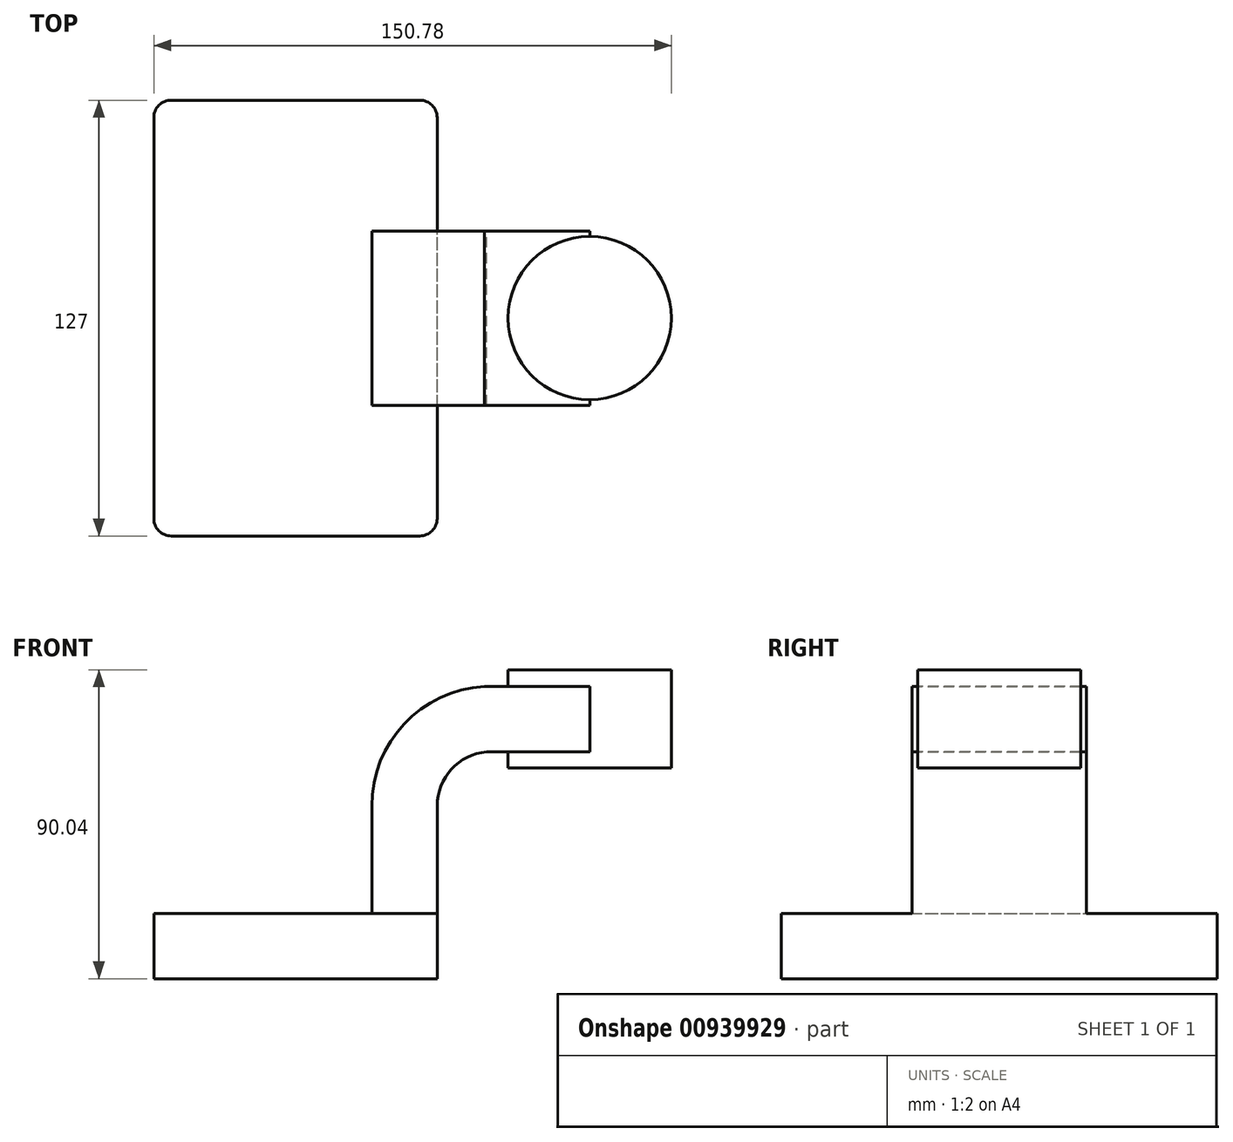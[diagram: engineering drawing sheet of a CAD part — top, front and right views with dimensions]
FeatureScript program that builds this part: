
annotation { "Feature Type Name" : "Feature", "Feature Type Description" : "" }
export const myFeature = defineFeature(function(context is Context, id is Id, definition is map)
    precondition{}
    {
        {
            var Q0;
            Q0=qCreatedBy(makeId("Front.planeOp"),FACE);
            var sketch = newSketch(context, id + "F0", { "sketchPlane" : qUnion([Q0])});
            skLineSegment(sketch, "E0.bottom", {"start": v(41.27, 9.53) * mm, "end": v(-41.28, 9.53) * mm});
            skLineSegment(sketch, "E0.top", {"start": v(41.28, -9.52) * mm, "end": v(-41.27, -9.52) * mm});
            skLineSegment(sketch, "E0.left", {"start": v(41.28, 9.53) * mm, "end": v(41.28, -9.52) * mm});
            skLineSegment(sketch, "E0.right", {"start": v(-41.28, 9.53) * mm, "end": v(-41.27, -9.52) * mm});
            skPoint(sketch, "E0.middle", {"position": v(0, 0) * mm});
            skLineSegment(sketch, "E1", {"start": v(41.27, 9.53) * mm, "end": v(41.27, 40.78) * mm});
            skArc(sketch, "E2", {"start": v(41.27, 40.78) * mm, "mid": v(45.42, 51.48) * mm, "end": v(55.7, 56.6) * mm});
            skLineSegment(sketch, "E3", {"start": v(55.7, 56.6) * mm, "end": v(85.73, 56.6) * mm});
            skPoint(sketch, "E4.middle", {"position": v(72.16, 48.26) * mm});
            skLineSegment(sketch, "E5.0", {"start": v(55, 75.64) * mm, "end": v(85.73, 75.64) * mm});
            skArc(sketch, "E5.1", {"start": v(22.23, 40.78) * mm, "mid": v(31.7, 64.7) * mm, "end": v(55, 75.64) * mm});
            skLineSegment(sketch, "E5.2", {"start": v(22.23, 9.53) * mm, "end": v(22.23, 40.78) * mm});
            skLineSegment(sketch, "E6.bottom", {"start": v(58.7, 51.93) * mm, "end": v(109.5, 51.93) * mm});
            skLineSegment(sketch, "E6.top", {"start": v(58.7, 80.5) * mm, "end": v(109.5, 80.5) * mm});
            skLineSegment(sketch, "E6.left", {"start": v(58.7, 51.93) * mm, "end": v(58.7, 80.5) * mm});
            skLineSegment(sketch, "E6.right", {"start": v(109.5, 51.93) * mm, "end": v(109.5, 80.5) * mm});
            skLineSegment(sketch, "E7", {"start": v(85.73, 80.5) * mm, "end": v(85.73, 51.93) * mm});
            skFitSpline(sketch, "E8", {"points": [v(-41.28, 9.53) * mm, v(58.7, 80.5) * mm], "startDerivative": vector(30.6, 76.42) * mm, "endDerivative": vector(213.62, 12.05) * mm});
            skSolve(sketch);
        }
        {
            var Q0;
            Q0=makeQuery(id+"F0.imprint","IMPRINT",FACE,{"disambiguationData":[TD([[makeQuery(id+"F0.imprint","IMPRINT",EDGE,{"derivedFrom":sQuery(id+"F0.wireOp",EDGE,"E0.top")}),-1.0]])]});
            extrude(context, id + "F1", {"entities" : qUnion([Q0]), "depth" : 127 * mm, "offsetDistance" : 25.4 * mm, "symmetric" : true});
        }
        {
            var Q0;
            {var subQ6=sQuery(id+"F0.wireOp",EDGE,"E1");Q0=makeQuery(id+"F0.imprint","IMPRINT",FACE,{"disambiguationData":[TD([[makeQuery(id+"F0.imprint","IMPRINT",EDGE,{"derivedFrom":subQ6}),1.0]])]});}
            var Q1;
            {var subQ0=sQuery(id+"F0.wireOp",EDGE,"E7");var subQ1=sQuery(id+"F0.wireOp",EDGE,"E3");var subQ2=makeQuery(id+"F0.imprint","INTERSECT",VERTEX,{"derivedFrom":[subQ1,subQ0]});Q1=makeQuery(id+"F0.imprint","IMPRINT",FACE,{"disambiguationData":[TD([[makeQuery(id+"F0.imprint","IMPRINT",EDGE,{"disambiguationData":[TD([[subQ2,1.0]])],"derivedFrom":subQ1}),1.0]])]});}
            extrude(context, id + "F2", {"entities" : qUnion([Q0, Q1]), "operationType" : NewBodyOperationType.ADD, "depth" : 50.8 * mm, "offsetDistance" : 25.4 * mm, "symmetric" : true});
        }
        {
            var Q0;
            {var subQ3=sQuery(id+"F0.wireOp",EDGE,"E5.1");Q0=makeQuery(id+"F0.imprint","IMPRINT",FACE,{"disambiguationData":[TD([[makeQuery(id+"F0.imprint","IMPRINT",EDGE,{"derivedFrom":subQ3}),1.0]])]});}
            extrude(context, id + "F3", {"entities" : qUnion([Q0]), "operationType" : NewBodyOperationType.ADD, "depth" : 15.88 * mm, "offsetDistance" : 25.4 * mm, "symmetric" : true});
        }
        {
            var Q0;
            {var subQ0=sQuery(id+"F0.wireOp",EDGE,"E6.right");Q0=makeQuery(id+"F0.imprint","IMPRINT",FACE,{"disambiguationData":[TD([[makeQuery(id+"F0.imprint","IMPRINT",EDGE,{"derivedFrom":subQ0}),1.0]])]});}
            var Q1;
            Q1=sQuery(id+"F0.wireOp",EDGE,"E7");
            revolve(context, id + "F4", {"operationType" : NewBodyOperationType.ADD, "surfaceOperationType" : NewSurfaceOperationType.NEW, "entities" : qUnion([Q0]), "axis" : qUnion([Q1]), "revolveType" : RevolveType.FULL});
        }
        {
            var Q0;
            Q0=makeQuery(id+"F1.opExtrude","CAP_EDGE",EDGE,{"disambiguationData":[OSD([sQuery(id+"F0.wireOp",EDGE,"E0.left")])],"isStart":true});
            var Q1;
            Q1=makeQuery(id+"F1.opExtrude","CAP_EDGE",EDGE,{"disambiguationData":[OSD([sQuery(id+"F0.wireOp",EDGE,"E0.right")])],"isStart":true});
            var Q2;
            Q2=makeQuery(id+"F1.opExtrude","CAP_EDGE",EDGE,{"disambiguationData":[OSD([sQuery(id+"F0.wireOp",EDGE,"E0.right")])],"isStart":false});
            var Q3;
            Q3=makeQuery(id+"F1.opExtrude","CAP_EDGE",EDGE,{"disambiguationData":[OSD([sQuery(id+"F0.wireOp",EDGE,"E0.left")])],"isStart":false});
            fillet(context, id + "F5", {"entities" : qUnion([Q0, Q1, Q2, Q3]), "radius" : 5.08 * mm, "tangentPropagation" : true, "allowEdgeOverflow" : false});
        }
    });
